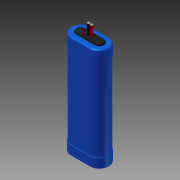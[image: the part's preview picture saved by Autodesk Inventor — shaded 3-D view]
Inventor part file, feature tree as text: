
AUTODESK INVENTOR PART (.ipt)
format: ipt  version: 2012 (Build 160160000, 160)  size: 153,600 bytes
history: native  units: in
note: dims shown in document units (in); Inventor stores cm internally (conversion verified against a paired STEP export)
features: other x1, imported_body x1, plane x1, split x1
ambient origin geometry x8: Origin, YZ Plane, XZ Plane, XY Plane, X Axis, Y Axis, Z Axis, Center Point
feature tree (4):
  parser-record x1  (decoder bookkeeping rows leaked as tree rows — omitted from the tree; the rows remain in map.json)
  imported_body  "Base1"
  plane  "Work Plane1"
  split  "Split1"
